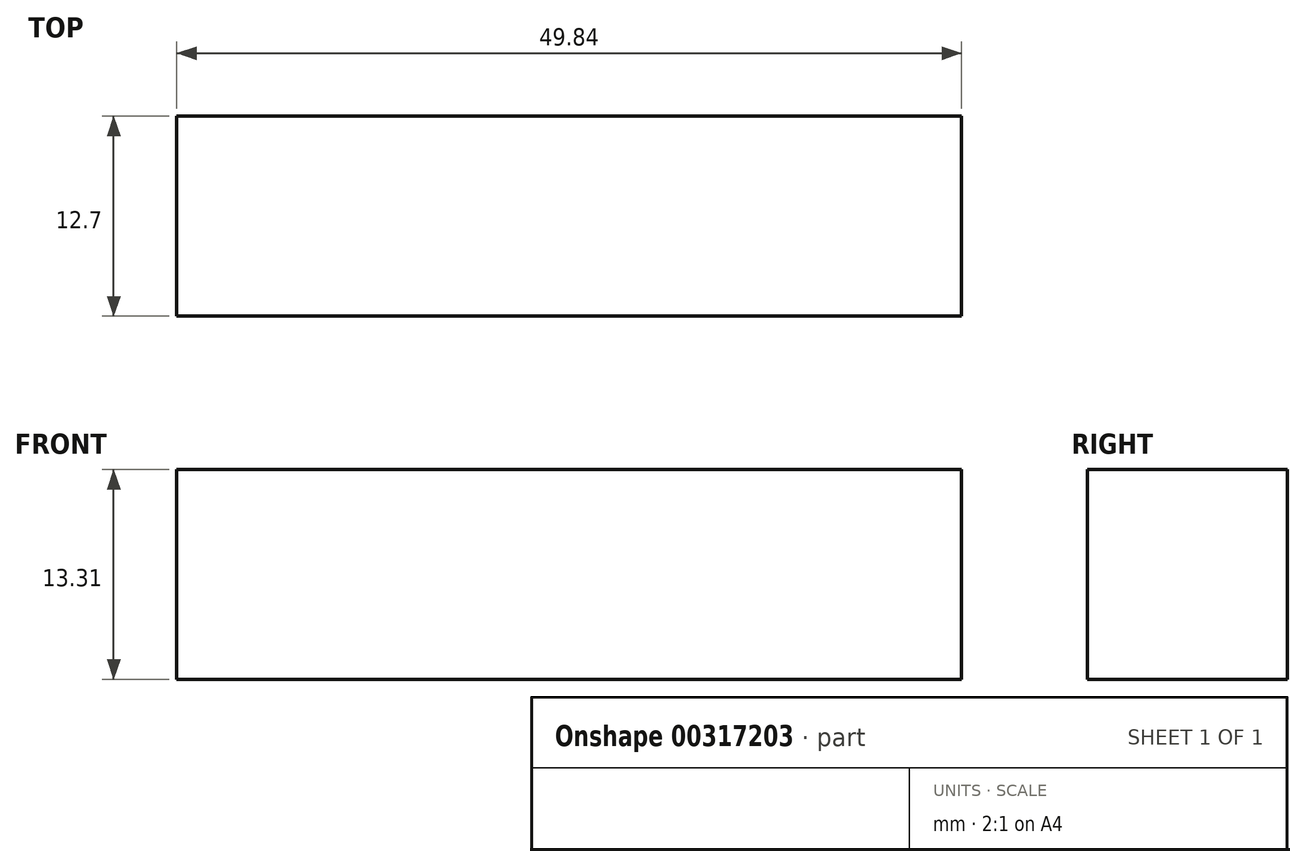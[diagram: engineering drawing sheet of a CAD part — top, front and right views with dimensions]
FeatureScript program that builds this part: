
annotation { "Feature Type Name" : "Feature", "Feature Type Description" : "" }
export const myFeature = defineFeature(function(context is Context, id is Id, definition is map)
    precondition{}
    {
        {
            var Q0;
            Q0=qCreatedBy(makeId("Front.planeOp"),FACE);
            var sketch = newSketch(context, id + "F0", { "sketchPlane" : qUnion([Q0])});
            skLineSegment(sketch, "E0.bottom", {"start": v(-27.86, 7.27) * mm, "end": v(21.98, 7.27) * mm});
            skLineSegment(sketch, "E0.top", {"start": v(-27.86, -6.04) * mm, "end": v(21.98, -6.04) * mm});
            skLineSegment(sketch, "E0.left", {"start": v(-27.86, 7.27) * mm, "end": v(-27.86, -6.04) * mm});
            skLineSegment(sketch, "E0.right", {"start": v(21.98, 7.27) * mm, "end": v(21.98, -6.04) * mm});
            skSolve(sketch);
        }
        {
            var Q0;
            Q0=makeQuery(id+"F0.imprint","IMPRINT",FACE,{"disambiguationData":[TD([[makeQuery(id+"F0.imprint","IMPRINT",EDGE,{"derivedFrom":sQuery(id+"F0.wireOp",EDGE,"E0.bottom")}),-1.0]])]});
            extrude(context, id + "F1", {"entities" : qUnion([Q0]), "depth" : 12.7 * mm});
        }
    });
